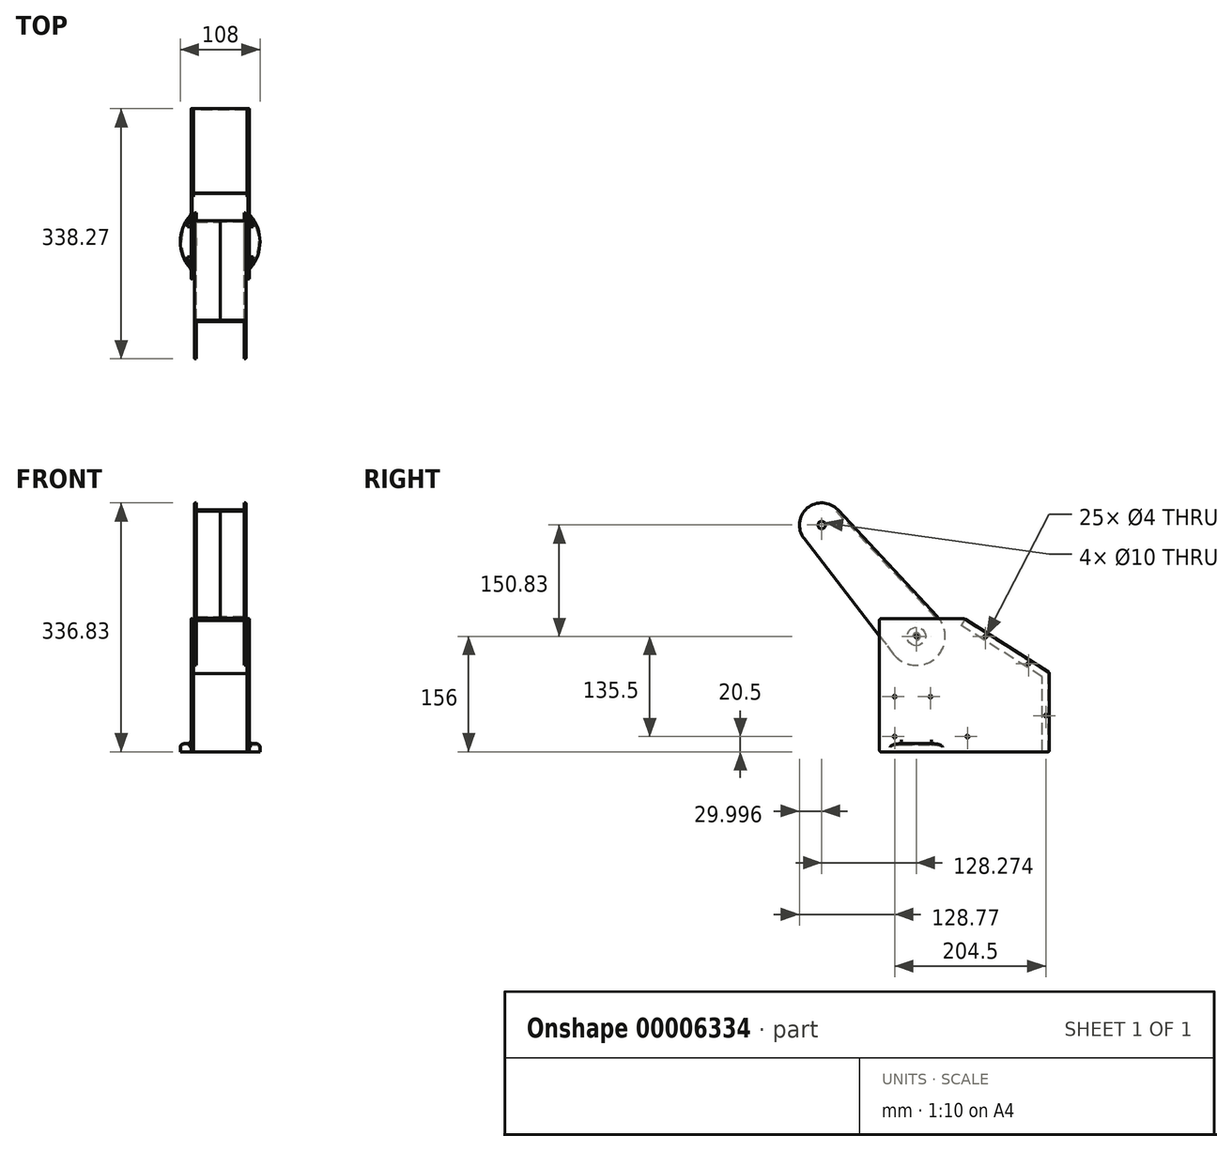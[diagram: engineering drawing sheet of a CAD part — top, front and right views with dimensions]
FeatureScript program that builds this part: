
annotation { "Feature Type Name" : "Feature", "Feature Type Description" : "" }
export const myFeature = defineFeature(function(context is Context, id is Id, definition is map)
    precondition{}
    {
        {
            var Q0;
            Q0=qCreatedBy(makeId("Right.planeOp"),FACE);
            var sketch = newSketch(context, id + "F0", { "sketchPlane" : qUnion([Q0])});
            skLineSegment(sketch, "E0", {"start": v(0, 2) * mm, "end": v(0, 178) * mm});
            skLineSegment(sketch, "E1", {"start": v(2, 180) * mm, "end": v(113.55, 180) * mm});
            skLineSegment(sketch, "E2", {"start": v(116.23, 179.22) * mm, "end": v(229.07, 107.59) * mm});
            skLineSegment(sketch, "E3", {"start": v(230, 105.9) * mm, "end": v(230, 2) * mm});
            skLineSegment(sketch, "E4", {"start": v(228, 0) * mm, "end": v(2, 0) * mm});
            skCircle(sketch, "E5", {"center": v(143.48, 156) * mm, "radius": 2 * mm});
            skCircle(sketch, "E6", {"center": v(201.5, 119.17) * mm, "radius": 2 * mm});
            skCircle(sketch, "E7", {"center": v(225, 49) * mm, "radius": 2 * mm});
            skLineSegment(sketch, "E8", {"start": v(230, 101.08) * mm, "end": v(105.67, 180) * mm, "construction": true});
            skLineSegment(sketch, "E9", {"start": v(225, 110.17) * mm, "end": v(225, 0) * mm, "construction": true});
            skCircle(sketch, "E10", {"center": v(50, 156) * mm, "radius": 2 * mm});
            skCircle(sketch, "E11", {"center": v(20.5, 74.5) * mm, "radius": 2 * mm});
            skCircle(sketch, "E12", {"center": v(69, 74.5) * mm, "radius": 2 * mm});
            skCircle(sketch, "E13", {"center": v(119, 20.5) * mm, "radius": 2 * mm});
            skLineSegment(sketch, "E14", {"start": v(20.5, 180) * mm, "end": v(20.5, 0) * mm, "construction": true});
            skLineSegment(sketch, "E15", {"start": v(0, 20.5) * mm, "end": v(230, 20.5) * mm, "construction": true});
            skCircle(sketch, "E16", {"center": v(20.5, 20.5) * mm, "radius": 2 * mm});
            skLineSegment(sketch, "E17", {"start": v(0, 74.5) * mm, "end": v(69, 74.5) * mm, "construction": true});
            skPoint(sketch, "E18.visualSharp", {"position": v(115, 180) * mm});
            skArc(sketch, "E18.filletArc", {"start": v(116.23, 179.22) * mm, "mid": v(114.94, 179.8) * mm, "end": v(113.55, 180) * mm});
            skPoint(sketch, "E19.visualSharp", {"position": v(0, 180) * mm});
            skArc(sketch, "E19.filletArc", {"start": v(2, 180) * mm, "mid": v(0.59, 179.41) * mm, "end": v(0, 178) * mm});
            skPoint(sketch, "E20.visualSharp", {"position": v(0, 0) * mm});
            skArc(sketch, "E20.filletArc", {"start": v(0, 2) * mm, "mid": v(0.59, 0.59) * mm, "end": v(2, 0) * mm});
            skPoint(sketch, "E21.visualSharp", {"position": v(230, 0) * mm});
            skArc(sketch, "E21.filletArc", {"start": v(228, 0) * mm, "mid": v(229.41, 0.59) * mm, "end": v(230, 2) * mm});
            skPoint(sketch, "E22.visualSharp", {"position": v(230, 107) * mm});
            skArc(sketch, "E22.filletArc", {"start": v(230, 105.9) * mm, "mid": v(229.75, 106.86) * mm, "end": v(229.07, 107.59) * mm});
            skLineSegment(sketch, "E23", {"start": v(0, 156) * mm, "end": v(152.8, 156) * mm, "construction": true});
            skSolve(sketch);
        }
        {
            var Q0;
            Q0=makeQuery(id+"F0.imprint","IMPRINT",FACE,{"disambiguationData":[TD([[makeQuery(id+"F0.imprint","IMPRINT",EDGE,{"derivedFrom":sQuery(id+"F0.wireOp",EDGE,"E0")}),-1.0]])]});
            extrude(context, id + "F1", {"entities" : qUnion([Q0]), "depth" : 1.7 * mm});
        }
        {
            var Q0;
            Q0=makeQuery(id+"F1.opExtrude","CAP_FACE",FACE,{"disambiguationData":[OSD([sQuery(id+"F0.wireOp",EDGE,"E0"),sQuery(id+"F0.wireOp",EDGE,"E1"),sQuery(id+"F0.wireOp",EDGE,"E2"),sQuery(id+"F0.wireOp",EDGE,"E3"),sQuery(id+"F0.wireOp",EDGE,"E4"),sQuery(id+"F0.wireOp",EDGE,"E5"),sQuery(id+"F0.wireOp",EDGE,"E6"),sQuery(id+"F0.wireOp",EDGE,"E7"),sQuery(id+"F0.wireOp",EDGE,"E10"),sQuery(id+"F0.wireOp",EDGE,"E11"),sQuery(id+"F0.wireOp",EDGE,"E12"),sQuery(id+"F0.wireOp",EDGE,"E13"),sQuery(id+"F0.wireOp",EDGE,"E16"),sQuery(id+"F0.wireOp",EDGE,"E18.filletArc"),sQuery(id+"F0.wireOp",EDGE,"E19.filletArc"),sQuery(id+"F0.wireOp",EDGE,"E20.filletArc"),sQuery(id+"F0.wireOp",EDGE,"E21.filletArc"),sQuery(id+"F0.wireOp",EDGE,"E22.filletArc")])],"isStart":true});
            cPlane(context, id + "F2", {"entities" : qUnion([Q0]), "cplaneType" : CPlaneType.OFFSET, "offset" : (79 / 2) * mm, "oppositeDirection" : true, "width" : 150 * mm, "height" : 150 * mm});
        }
        {
            var Q0;
            Q0=qCreatedBy(makeId("Top.planeOp"),FACE);
            var sketch = newSketch(context, id + "F3", { "sketchPlane" : qUnion([Q0])});
            skCircle(sketch, "E24", {"center": v(39.5, 50) * mm, "radius": 54 * mm});
            skSolve(sketch);
        }
        {
            var Q0;
            Q0=makeQuery(id+"F3.imprint","IMPRINT",FACE,{"disambiguationData":[TD([[makeQuery(id+"F3.imprint","IMPRINT",EDGE,{"derivedFrom":sQuery(id+"F3.wireOp",EDGE,"E24")}),1.0]])]});
            extrude(context, id + "F4", {"entities" : qUnion([Q0]), "operationType" : NewBodyOperationType.ADD, "depth" : 11 * mm});
        }
        {
            var Q0;
            {var subQ0=sQuery(id+"F3.wireOp",EDGE,"E24");Q0=makeQuery(id+"F4.boolean.opBoolean","SPLIT",FACE,{"disambiguationData":[TD([makeQuery(id+"F1.opExtrude","CAP_FACE",FACE,{"disambiguationData":[OSD([sQuery(id+"F0.wireOp",EDGE,"E0"),sQuery(id+"F0.wireOp",EDGE,"E1"),sQuery(id+"F0.wireOp",EDGE,"E2"),sQuery(id+"F0.wireOp",EDGE,"E3"),sQuery(id+"F0.wireOp",EDGE,"E4"),sQuery(id+"F0.wireOp",EDGE,"E5"),sQuery(id+"F0.wireOp",EDGE,"E6"),sQuery(id+"F0.wireOp",EDGE,"E7"),sQuery(id+"F0.wireOp",EDGE,"E10"),sQuery(id+"F0.wireOp",EDGE,"E11"),sQuery(id+"F0.wireOp",EDGE,"E12"),sQuery(id+"F0.wireOp",EDGE,"E13"),sQuery(id+"F0.wireOp",EDGE,"E16"),sQuery(id+"F0.wireOp",EDGE,"E18.filletArc"),sQuery(id+"F0.wireOp",EDGE,"E19.filletArc"),sQuery(id+"F0.wireOp",EDGE,"E20.filletArc"),sQuery(id+"F0.wireOp",EDGE,"E21.filletArc"),sQuery(id+"F0.wireOp",EDGE,"E22.filletArc")])],"isStart":false})])],"derivedFrom":makeQuery(id+"F4.opExtrude","CAP_FACE",FACE,{"disambiguationData":[OSD([subQ0])],"isStart":false})});}
            extrude(context, id + "F5", {"entities" : qUnion([Q0]), "operationType" : NewBodyOperationType.REMOVE, "endBound" : BoundingType.UP_TO_NEXT, "oppositeDirection" : true, "depth" : 25 * mm});
        }
        {
            var Q0;
            Q0=makeQuery(id+"F4.boolean.opBoolean","INTERSECT",EDGE,{"disambiguationData":[OD(1.0)],"derivedFrom":[makeQuery(id+"F1.opExtrude","CAP_FACE",FACE,{"disambiguationData":[OSD([sQuery(id+"F0.wireOp",EDGE,"E0"),sQuery(id+"F0.wireOp",EDGE,"E1"),sQuery(id+"F0.wireOp",EDGE,"E2"),sQuery(id+"F0.wireOp",EDGE,"E3"),sQuery(id+"F0.wireOp",EDGE,"E4"),sQuery(id+"F0.wireOp",EDGE,"E5"),sQuery(id+"F0.wireOp",EDGE,"E6"),sQuery(id+"F0.wireOp",EDGE,"E7"),sQuery(id+"F0.wireOp",EDGE,"E10"),sQuery(id+"F0.wireOp",EDGE,"E11"),sQuery(id+"F0.wireOp",EDGE,"E12"),sQuery(id+"F0.wireOp",EDGE,"E13"),sQuery(id+"F0.wireOp",EDGE,"E16"),sQuery(id+"F0.wireOp",EDGE,"E18.filletArc"),sQuery(id+"F0.wireOp",EDGE,"E19.filletArc"),sQuery(id+"F0.wireOp",EDGE,"E20.filletArc"),sQuery(id+"F0.wireOp",EDGE,"E21.filletArc"),sQuery(id+"F0.wireOp",EDGE,"E22.filletArc")])],"isStart":true}),makeQuery(id+"F4.opExtrude","SWEPT_FACE",FACE,{"disambiguationData":[OSD([sQuery(id+"F3.wireOp",EDGE,"E24")])]})]});
            var Q1;
            Q1=makeQuery(id+"F4.boolean.opBoolean","INTERSECT",EDGE,{"derivedFrom":[makeQuery(id+"F1.opExtrude","CAP_FACE",FACE,{"disambiguationData":[OSD([sQuery(id+"F0.wireOp",EDGE,"E0"),sQuery(id+"F0.wireOp",EDGE,"E1"),sQuery(id+"F0.wireOp",EDGE,"E2"),sQuery(id+"F0.wireOp",EDGE,"E3"),sQuery(id+"F0.wireOp",EDGE,"E4"),sQuery(id+"F0.wireOp",EDGE,"E5"),sQuery(id+"F0.wireOp",EDGE,"E6"),sQuery(id+"F0.wireOp",EDGE,"E7"),sQuery(id+"F0.wireOp",EDGE,"E10"),sQuery(id+"F0.wireOp",EDGE,"E11"),sQuery(id+"F0.wireOp",EDGE,"E12"),sQuery(id+"F0.wireOp",EDGE,"E13"),sQuery(id+"F0.wireOp",EDGE,"E16"),sQuery(id+"F0.wireOp",EDGE,"E18.filletArc"),sQuery(id+"F0.wireOp",EDGE,"E19.filletArc"),sQuery(id+"F0.wireOp",EDGE,"E20.filletArc"),sQuery(id+"F0.wireOp",EDGE,"E21.filletArc"),sQuery(id+"F0.wireOp",EDGE,"E22.filletArc")])],"isStart":true}),makeQuery(id+"F4.opExtrude","CAP_FACE",FACE,{"disambiguationData":[OSD([sQuery(id+"F3.wireOp",EDGE,"E24")])],"isStart":false})]});
            var Q2;
            Q2=makeQuery(id+"F4.boolean.opBoolean","INTERSECT",EDGE,{"disambiguationData":[OD(0.0)],"derivedFrom":[makeQuery(id+"F1.opExtrude","CAP_FACE",FACE,{"disambiguationData":[OSD([sQuery(id+"F0.wireOp",EDGE,"E0"),sQuery(id+"F0.wireOp",EDGE,"E1"),sQuery(id+"F0.wireOp",EDGE,"E2"),sQuery(id+"F0.wireOp",EDGE,"E3"),sQuery(id+"F0.wireOp",EDGE,"E4"),sQuery(id+"F0.wireOp",EDGE,"E5"),sQuery(id+"F0.wireOp",EDGE,"E6"),sQuery(id+"F0.wireOp",EDGE,"E7"),sQuery(id+"F0.wireOp",EDGE,"E10"),sQuery(id+"F0.wireOp",EDGE,"E11"),sQuery(id+"F0.wireOp",EDGE,"E12"),sQuery(id+"F0.wireOp",EDGE,"E13"),sQuery(id+"F0.wireOp",EDGE,"E16"),sQuery(id+"F0.wireOp",EDGE,"E18.filletArc"),sQuery(id+"F0.wireOp",EDGE,"E19.filletArc"),sQuery(id+"F0.wireOp",EDGE,"E20.filletArc"),sQuery(id+"F0.wireOp",EDGE,"E21.filletArc"),sQuery(id+"F0.wireOp",EDGE,"E22.filletArc")])],"isStart":true}),makeQuery(id+"F4.opExtrude","SWEPT_FACE",FACE,{"disambiguationData":[OSD([sQuery(id+"F3.wireOp",EDGE,"E24")])]})]});
            var Q3;
            {var subQ0=sQuery(id+"F3.wireOp",EDGE,"E24");Q3=makeQuery(id+"F4.boolean.opBoolean","SPLIT",EDGE,{"disambiguationData":[TD([makeQuery(id+"F1.opExtrude","CAP_FACE",FACE,{"disambiguationData":[OSD([sQuery(id+"F0.wireOp",EDGE,"E0"),sQuery(id+"F0.wireOp",EDGE,"E1"),sQuery(id+"F0.wireOp",EDGE,"E2"),sQuery(id+"F0.wireOp",EDGE,"E3"),sQuery(id+"F0.wireOp",EDGE,"E4"),sQuery(id+"F0.wireOp",EDGE,"E5"),sQuery(id+"F0.wireOp",EDGE,"E6"),sQuery(id+"F0.wireOp",EDGE,"E7"),sQuery(id+"F0.wireOp",EDGE,"E10"),sQuery(id+"F0.wireOp",EDGE,"E11"),sQuery(id+"F0.wireOp",EDGE,"E12"),sQuery(id+"F0.wireOp",EDGE,"E13"),sQuery(id+"F0.wireOp",EDGE,"E16"),sQuery(id+"F0.wireOp",EDGE,"E18.filletArc"),sQuery(id+"F0.wireOp",EDGE,"E19.filletArc"),sQuery(id+"F0.wireOp",EDGE,"E20.filletArc"),sQuery(id+"F0.wireOp",EDGE,"E21.filletArc"),sQuery(id+"F0.wireOp",EDGE,"E22.filletArc")])],"isStart":true})])],"derivedFrom":makeQuery(id+"F4.opExtrude","CAP_EDGE",EDGE,{"disambiguationData":[OSD([subQ0])],"isStart":false})});}
            fillet(context, id + "F6", {"entities" : qUnion([Q0, Q1, Q2, Q3]), "radius" : 5 * mm, "tangentPropagation" : true, "allowEdgeOverflow" : false});
        }
        {
            var Q0;
            {var subQ0=sQuery(id+"F0.wireOp",EDGE,"E22.filletArc");var subQ1=sQuery(id+"F0.wireOp",EDGE,"E21.filletArc");var subQ2=sQuery(id+"F0.wireOp",EDGE,"E20.filletArc");var subQ3=sQuery(id+"F0.wireOp",EDGE,"E19.filletArc");var subQ4=sQuery(id+"F0.wireOp",EDGE,"E18.filletArc");var subQ5=sQuery(id+"F0.wireOp",EDGE,"E16");var subQ6=sQuery(id+"F0.wireOp",EDGE,"E13");var subQ7=sQuery(id+"F0.wireOp",EDGE,"E12");var subQ8=sQuery(id+"F0.wireOp",EDGE,"E11");var subQ9=sQuery(id+"F0.wireOp",EDGE,"E10");var subQ10=sQuery(id+"F0.wireOp",EDGE,"E7");var subQ11=sQuery(id+"F0.wireOp",EDGE,"E6");var subQ12=sQuery(id+"F0.wireOp",EDGE,"E5");var subQ13=sQuery(id+"F0.wireOp",EDGE,"E4");var subQ14=sQuery(id+"F0.wireOp",EDGE,"E3");var subQ15=sQuery(id+"F0.wireOp",EDGE,"E2");var subQ16=sQuery(id+"F0.wireOp",EDGE,"E1");var subQ17=sQuery(id+"F0.wireOp",EDGE,"E0");Q0=makeQuery(id+"F5.boolean.opBoolean","MERGE",FACE,{"derivedFrom":[makeQuery(id+"F1.opExtrude","CAP_FACE",FACE,{"disambiguationData":[OSD([subQ17,subQ16,subQ15,subQ14,subQ13,subQ12,subQ11,subQ10,subQ9,subQ8,subQ7,subQ6,subQ5,subQ4,subQ3,subQ2,subQ1,subQ0])],"isStart":false})],"fromTools":[makeQuery(id+"F5.opExtrude","SWEPT_FACE",FACE,{"disambiguationData":[OSD([subQ17,subQ16,subQ15,subQ14,subQ13,subQ12,subQ11,subQ10,subQ9,subQ8,subQ7,subQ6,subQ5,subQ4,subQ3,subQ2,subQ1,subQ0,sQuery(id+"F3.wireOp",EDGE,"E24")])]})]});}
            var Q1;
            Q1=makeQuery(id+"F4.boolean.opBoolean","MERGE",FACE,{"derivedFrom":[makeQuery(id+"F1.opExtrude","SWEPT_FACE",FACE,{"disambiguationData":[OSD([sQuery(id+"F0.wireOp",EDGE,"E4")])]}),makeQuery(id+"F4.opExtrude","CAP_FACE",FACE,{"disambiguationData":[OSD([sQuery(id+"F3.wireOp",EDGE,"E24")])],"isStart":true})]});
            shell(context, id + "F7", {"entities" : qUnion([Q0, Q1]), "thickness" : 1.7 * mm});
        }
        {
            var Q0;
            {var subQ0=sQuery(id+"F0.wireOp",EDGE,"E22.filletArc");var subQ1=sQuery(id+"F0.wireOp",EDGE,"E21.filletArc");var subQ2=sQuery(id+"F0.wireOp",EDGE,"E20.filletArc");var subQ3=sQuery(id+"F0.wireOp",EDGE,"E19.filletArc");var subQ4=sQuery(id+"F0.wireOp",EDGE,"E18.filletArc");var subQ5=sQuery(id+"F0.wireOp",EDGE,"E16");var subQ6=sQuery(id+"F0.wireOp",EDGE,"E13");var subQ7=sQuery(id+"F0.wireOp",EDGE,"E12");var subQ8=sQuery(id+"F0.wireOp",EDGE,"E11");var subQ9=sQuery(id+"F0.wireOp",EDGE,"E10");var subQ10=sQuery(id+"F0.wireOp",EDGE,"E7");var subQ11=sQuery(id+"F0.wireOp",EDGE,"E6");var subQ12=sQuery(id+"F0.wireOp",EDGE,"E5");var subQ13=sQuery(id+"F0.wireOp",EDGE,"E4");var subQ14=sQuery(id+"F0.wireOp",EDGE,"E3");var subQ15=sQuery(id+"F0.wireOp",EDGE,"E2");var subQ16=sQuery(id+"F0.wireOp",EDGE,"E1");var subQ17=sQuery(id+"F0.wireOp",EDGE,"E0");Q0=makeQuery(id+"F5.boolean.opBoolean","MERGE",FACE,{"derivedFrom":[makeQuery(id+"F1.opExtrude","CAP_FACE",FACE,{"disambiguationData":[OSD([subQ17,subQ16,subQ15,subQ14,subQ13,subQ12,subQ11,subQ10,subQ9,subQ8,subQ7,subQ6,subQ5,subQ4,subQ3,subQ2,subQ1,subQ0])],"isStart":false})],"fromTools":[makeQuery(id+"F5.opExtrude","SWEPT_FACE",FACE,{"disambiguationData":[OSD([subQ17,subQ16,subQ15,subQ14,subQ13,subQ12,subQ11,subQ10,subQ9,subQ8,subQ7,subQ6,subQ5,subQ4,subQ3,subQ2,subQ1,subQ0,sQuery(id+"F3.wireOp",EDGE,"E24")])]})]});}
            var sketch = newSketch(context, id + "F8", { "sketchPlane" : qUnion([Q0])});
            skLineSegment(sketch, "E25", {"start": v(116.23, 179.22) * mm, "end": v(230, 107) * mm});
            skLineSegment(sketch, "E26", {"start": v(230, 107) * mm, "end": v(230, 0) * mm});
            skLineSegment(sketch, "E27", {"start": v(230, 0) * mm, "end": v(220, 0) * mm});
            skLineSegment(sketch, "E28", {"start": v(220, 0) * mm, "end": v(220, 101.5) * mm});
            skLineSegment(sketch, "E29", {"start": v(220, 101.5) * mm, "end": v(110.87, 170.78) * mm});
            skLineSegment(sketch, "E30", {"start": v(110.87, 170.78) * mm, "end": v(116.23, 179.22) * mm});
            skCircle(sketch, "E31", {"center": v(143.48, 156) * mm, "radius": 2 * mm});
            skCircle(sketch, "E32", {"center": v(201.5, 119.17) * mm, "radius": 2 * mm});
            skCircle(sketch, "E33", {"center": v(225, 49) * mm, "radius": 2 * mm});
            skSolve(sketch);
        }
        {
            var Q0;
            {var subQ5=sQuery(id+"F8.wireOp",EDGE,"E28");Q0=makeQuery(id+"F8.imprint","IMPRINT",FACE,{"disambiguationData":[TD([[makeQuery(id+"F8.imprint","IMPRINT",EDGE,{"derivedFrom":subQ5}),-1.0]])]});}
            extrude(context, id + "F9", {"entities" : qUnion([Q0]), "depth" : 1.7 * mm});
        }
        {
            var Q0;
            {var subQ0=sQuery(id+"F0.wireOp",EDGE,"E22.filletArc");var subQ1=sQuery(id+"F0.wireOp",EDGE,"E21.filletArc");var subQ2=sQuery(id+"F0.wireOp",EDGE,"E20.filletArc");var subQ3=sQuery(id+"F0.wireOp",EDGE,"E19.filletArc");var subQ4=sQuery(id+"F0.wireOp",EDGE,"E18.filletArc");var subQ5=sQuery(id+"F0.wireOp",EDGE,"E16");var subQ6=sQuery(id+"F0.wireOp",EDGE,"E13");var subQ7=sQuery(id+"F0.wireOp",EDGE,"E12");var subQ8=sQuery(id+"F0.wireOp",EDGE,"E11");var subQ9=sQuery(id+"F0.wireOp",EDGE,"E10");var subQ10=sQuery(id+"F0.wireOp",EDGE,"E7");var subQ11=sQuery(id+"F0.wireOp",EDGE,"E6");var subQ12=sQuery(id+"F0.wireOp",EDGE,"E5");var subQ13=sQuery(id+"F0.wireOp",EDGE,"E4");var subQ14=sQuery(id+"F0.wireOp",EDGE,"E3");var subQ15=sQuery(id+"F0.wireOp",EDGE,"E2");var subQ16=sQuery(id+"F0.wireOp",EDGE,"E1");var subQ17=sQuery(id+"F0.wireOp",EDGE,"E0");Q0=makeQuery(id+"F5.boolean.opBoolean","MERGE",FACE,{"derivedFrom":[makeQuery(id+"F1.opExtrude","CAP_FACE",FACE,{"disambiguationData":[OSD([subQ17,subQ16,subQ15,subQ14,subQ13,subQ12,subQ11,subQ10,subQ9,subQ8,subQ7,subQ6,subQ5,subQ4,subQ3,subQ2,subQ1,subQ0])],"isStart":false})],"fromTools":[makeQuery(id+"F5.opExtrude","SWEPT_FACE",FACE,{"disambiguationData":[OSD([subQ17,subQ16,subQ15,subQ14,subQ13,subQ12,subQ11,subQ10,subQ9,subQ8,subQ7,subQ6,subQ5,subQ4,subQ3,subQ2,subQ1,subQ0,sQuery(id+"F3.wireOp",EDGE,"E24")])]})]});}
            var sketch = newSketch(context, id + "F10", { "sketchPlane" : qUnion([Q0])});
            skCircle(sketch, "E34", {"center": v(50, 156) * mm, "radius": 2 * mm});
            skCircle(sketch, "E35", {"center": v(50, 156) * mm, "radius": 12.5 * mm});
            skSolve(sketch);
        }
        {
            var Q0;
            Q0=makeQuery(id+"F10.imprint","IMPRINT",FACE,{"disambiguationData":[TD([[makeQuery(id+"F10.imprint","IMPRINT",EDGE,{"derivedFrom":sQuery(id+"F10.wireOp",EDGE,"E34")}),-1.0]])]});
            extrude(context, id + "F11", {"entities" : qUnion([Q0]), "depth" : 3 * mm});
        }
        {
            var Q0;
            Q0=makeQuery(id+"F11.opExtrude","CAP_EDGE",EDGE,{"disambiguationData":[OSD([sQuery(id+"F10.wireOp",EDGE,"E35")])],"isStart":true});
            var Q1;
            Q1=makeQuery(id+"F11.opExtrude","CAP_EDGE",EDGE,{"disambiguationData":[OSD([sQuery(id+"F10.wireOp",EDGE,"E35")])],"isStart":false});
            fillet(context, id + "F12", {"entities" : qUnion([Q0, Q1]), "radius" : 1.5 * mm, "tangentPropagation" : true, "allowEdgeOverflow" : false});
        }
        {
            var Q0;
            Q0=makeQuery(id+"F1.opExtrude","SWEPT_BODY",BODY,{"disambiguationData":[OSD([sQuery(id+"F0.wireOp",EDGE,"E0"),sQuery(id+"F0.wireOp",EDGE,"E1"),sQuery(id+"F0.wireOp",EDGE,"E2"),sQuery(id+"F0.wireOp",EDGE,"E3"),sQuery(id+"F0.wireOp",EDGE,"E4"),sQuery(id+"F0.wireOp",EDGE,"E5"),sQuery(id+"F0.wireOp",EDGE,"E6"),sQuery(id+"F0.wireOp",EDGE,"E7"),sQuery(id+"F0.wireOp",EDGE,"E10"),sQuery(id+"F0.wireOp",EDGE,"E11"),sQuery(id+"F0.wireOp",EDGE,"E12"),sQuery(id+"F0.wireOp",EDGE,"E13"),sQuery(id+"F0.wireOp",EDGE,"E16"),sQuery(id+"F0.wireOp",EDGE,"E18.filletArc"),sQuery(id+"F0.wireOp",EDGE,"E19.filletArc"),sQuery(id+"F0.wireOp",EDGE,"E20.filletArc"),sQuery(id+"F0.wireOp",EDGE,"E21.filletArc"),sQuery(id+"F0.wireOp",EDGE,"E22.filletArc")])]});
            var Q1;
            Q1=makeQuery(id+"F9.opExtrude","SWEPT_BODY",BODY,{"disambiguationData":[OSD([sQuery(id+"F0.wireOp",EDGE,"E21.filletArc"),sQuery(id+"F0.wireOp",EDGE,"E22.filletArc"),sQuery(id+"F8.wireOp",EDGE,"E25"),sQuery(id+"F8.wireOp",EDGE,"E26"),sQuery(id+"F8.wireOp",EDGE,"E27"),sQuery(id+"F8.wireOp",EDGE,"E28"),sQuery(id+"F8.wireOp",EDGE,"E29"),sQuery(id+"F8.wireOp",EDGE,"E30"),sQuery(id+"F8.wireOp",EDGE,"E31"),sQuery(id+"F8.wireOp",EDGE,"E32"),sQuery(id+"F8.wireOp",EDGE,"E33")])]});
            var Q2;
            Q2=makeQuery(id+"F11.opExtrude","SWEPT_BODY",BODY,{"disambiguationData":[OSD([sQuery(id+"F10.wireOp",EDGE,"E34"),sQuery(id+"F10.wireOp",EDGE,"E35")])]});
            var Q3;
            Q3=qCreatedBy(id+"F2.planeOp",FACE);
            mirror(context, id + "F13", {"entities" : qUnion([Q0, Q1, Q2]), "mirrorPlane" : qUnion([Q3])});
        }
        {
            var Q0;
            Q0=makeQuery(id+"F9.opExtrude","CAP_FACE",FACE,{"disambiguationData":[OSD([sQuery(id+"F0.wireOp",EDGE,"E21.filletArc"),sQuery(id+"F0.wireOp",EDGE,"E22.filletArc"),sQuery(id+"F8.wireOp",EDGE,"E25"),sQuery(id+"F8.wireOp",EDGE,"E26"),sQuery(id+"F8.wireOp",EDGE,"E27"),sQuery(id+"F8.wireOp",EDGE,"E28"),sQuery(id+"F8.wireOp",EDGE,"E29"),sQuery(id+"F8.wireOp",EDGE,"E30"),sQuery(id+"F8.wireOp",EDGE,"E31"),sQuery(id+"F8.wireOp",EDGE,"E32"),sQuery(id+"F8.wireOp",EDGE,"E33")])],"isStart":false});
            var sketch = newSketch(context, id + "F14", { "sketchPlane" : qUnion([Q0])});
            skLineSegment(sketch, "E36", {"start": v(115.32, 177.79) * mm, "end": v(228.3, 106.07) * mm});
            skLineSegment(sketch, "E37", {"start": v(228.3, 106.07) * mm, "end": v(228.3, 0) * mm});
            skSolve(sketch);
        }
        {
            var Q0;
            Q0 = qSketchRegion(id + "F14", true);
            var Q1;
            {var subQ5=sQuery(id+"F14.wireOp",EDGE,"E36");Q1=makeQuery(id+"F14.imprint","IMPRINT",FACE,{"disambiguationData":[TD([[makeQuery(id+"F14.imprint","IMPRINT",EDGE,{"derivedFrom":subQ5}),1.0]])]});}
            var Q2;
            Q2=makeQuery(id+"F13.opPattern","COPY",FACE,{"derivedFrom":makeQuery(id+"F9.opExtrude","CAP_FACE",FACE,{"disambiguationData":[OSD([sQuery(id+"F0.wireOp",EDGE,"E21.filletArc"),sQuery(id+"F0.wireOp",EDGE,"E22.filletArc"),sQuery(id+"F8.wireOp",EDGE,"E25"),sQuery(id+"F8.wireOp",EDGE,"E26"),sQuery(id+"F8.wireOp",EDGE,"E27"),sQuery(id+"F8.wireOp",EDGE,"E28"),sQuery(id+"F8.wireOp",EDGE,"E29"),sQuery(id+"F8.wireOp",EDGE,"E30"),sQuery(id+"F8.wireOp",EDGE,"E31"),sQuery(id+"F8.wireOp",EDGE,"E32"),sQuery(id+"F8.wireOp",EDGE,"E33")])],"isStart":false}),"instanceName":"1"});
            extrude(context, id + "F15", {"entities" : qUnion([Q0, Q1]), "endBound" : BoundingType.UP_TO_SURFACE, "endBoundEntityFace" : qUnion([Q2]), "depth" : 25 * mm});
        }
        {
            var Q0;
            Q0=makeQuery(id+"F15.opExtrude","CAP_EDGE",EDGE,{"disambiguationData":[OSD([sQuery(id+"F14.wireOp",EDGE,"E36")])],"isStart":true});
            var Q1;
            Q1=makeQuery(id+"F9.opExtrude","CAP_EDGE",EDGE,{"disambiguationData":[OSD([sQuery(id+"F8.wireOp",EDGE,"E25")])],"isStart":true});
            var Q2;
            Q2=makeQuery(id+"F15.opExtrude","CAP_EDGE",EDGE,{"disambiguationData":[OSD([sQuery(id+"F14.wireOp",EDGE,"E37")])],"isStart":true});
            var Q3;
            Q3=makeQuery(id+"F9.opExtrude","CAP_EDGE",EDGE,{"disambiguationData":[OSD([sQuery(id+"F8.wireOp",EDGE,"E26")])],"isStart":true});
            var Q4;
            Q4=makeQuery(id+"F15.opExtrude","CAP_EDGE",EDGE,{"disambiguationData":[OSD([sQuery(id+"F14.wireOp",EDGE,"E36")])],"isStart":false});
            var Q5;
            Q5=makeQuery(id+"F15.opExtrude","CAP_EDGE",EDGE,{"disambiguationData":[OSD([sQuery(id+"F14.wireOp",EDGE,"E37")])],"isStart":false});
            var Q6;
            Q6=makeQuery(id+"F13.opPattern","COPY",EDGE,{"derivedFrom":makeQuery(id+"F9.opExtrude","CAP_EDGE",EDGE,{"disambiguationData":[OSD([sQuery(id+"F8.wireOp",EDGE,"E26")])],"isStart":true}),"instanceName":"1"});
            var Q7;
            Q7=makeQuery(id+"F13.opPattern","COPY",EDGE,{"derivedFrom":makeQuery(id+"F9.opExtrude","CAP_EDGE",EDGE,{"disambiguationData":[OSD([sQuery(id+"F8.wireOp",EDGE,"E25")])],"isStart":true}),"instanceName":"1"});
            fillet(context, id + "F16", {"entities" : qUnion([Q0, Q1, Q2, Q3, Q4, Q5, Q6, Q7]), "radius" : 1 * mm, "tangentPropagation" : true, "allowEdgeOverflow" : false});
        }
        {
            var Q0;
            Q0=makeQuery(id+"F11.opExtrude","SWEPT_BODY",BODY,{"disambiguationData":[OSD([sQuery(id+"F10.wireOp",EDGE,"E34"),sQuery(id+"F10.wireOp",EDGE,"E35")])]});
            var Q1;
            Q1=qCreatedBy(id+"F2.planeOp",FACE);
            mirror(context, id + "F17", {"entities" : qUnion([Q0]), "mirrorPlane" : qUnion([Q1])});
        }
        {
            var Q0;
            Q0=qCreatedBy(id+"F2.planeOp",FACE);
            var sketch = newSketch(context, id + "F18", { "sketchPlane" : qUnion([Q0])});
            skCircle(sketch, "E38", {"center": v(-50, 156) * mm, "radius": 5 * mm});
            skCircle(sketch, "E39", {"center": v(-50, 156) * mm, "radius": 2 * mm});
            skCircle(sketch, "E40", {"center": v(-50, 156) * mm, "radius": 39 * mm});
            skCircle(sketch, "E41", {"center": v(78.27, 306.83) * mm, "radius": 30 * mm});
            skCircle(sketch, "E42", {"center": v(78.27, 306.83) * mm, "radius": 5 * mm});
            skCircle(sketch, "E43", {"center": v(78.27, 306.83) * mm, "radius": 2 * mm});
            skLineSegment(sketch, "E44", {"start": v(-19.17, 132.11) * mm, "end": v(101.99, 288.45) * mm});
            skLineSegment(sketch, "E45", {"start": v(-78.53, 182.6) * mm, "end": v(56.33, 327.28) * mm});
            skCircle(sketch, "E46", {"center": v(221.31, 265.1) * mm, "radius": 2 * mm});
            skCircle(sketch, "E47", {"center": v(221.31, 265.1) * mm, "radius": 5 * mm});
            skCircle(sketch, "E48", {"center": v(221.31, 265.1) * mm, "radius": 20.5 * mm});
            skLineSegment(sketch, "E49", {"start": v(71.73, 277.55) * mm, "end": v(216.84, 245.1) * mm});
            skLineSegment(sketch, "E50", {"start": v(88.5, 335.04) * mm, "end": v(228.3, 284.38) * mm});
            skSolve(sketch);
        }
        {
            var Q0;
            Q0=makeQuery(id+"F18.imprint","IMPRINT",FACE,{"disambiguationData":[TD([[makeQuery(id+"F18.imprint","IMPRINT",EDGE,{"derivedFrom":sQuery(id+"F18.wireOp",EDGE,"E38")}),-1.0]])]});
            var Q1;
            {var subQ5=sQuery(id+"F18.wireOp",EDGE,"E45");Q1=makeQuery(id+"F18.imprint","IMPRINT",FACE,{"disambiguationData":[TD([[makeQuery(id+"F18.imprint","IMPRINT",EDGE,{"derivedFrom":subQ5}),-1.0]])]});}
            var Q2;
            Q2=makeQuery(id+"F18.imprint","IMPRINT",FACE,{"disambiguationData":[TD([[makeQuery(id+"F18.imprint","IMPRINT",EDGE,{"derivedFrom":sQuery(id+"F18.wireOp",EDGE,"E42")}),-1.0]])]});
            var Q3;
            {var subQ1=sQuery(id+"F18.wireOp",EDGE,"E44");var subQ3=sQuery(id+"F18.wireOp",EDGE,"E41");var subQ5=makeQuery(id+"F18.imprint","INTERSECT",VERTEX,{"derivedFrom":[subQ3,subQ1]});Q3=makeQuery(id+"F18.imprint","IMPRINT",FACE,{"disambiguationData":[TD([[makeQuery(id+"F18.imprint","IMPRINT",EDGE,{"disambiguationData":[TD([[subQ5,1.0]])],"derivedFrom":subQ3}),-1.0]])]});}
            var Q4;
            Q4=makeQuery(id+"F11.opExtrude","CAP_FACE",FACE,{"disambiguationData":[OSD([sQuery(id+"F10.wireOp",EDGE,"E34"),sQuery(id+"F10.wireOp",EDGE,"E35")])],"isStart":false});
            extrude(context, id + "F19", {"entities" : qUnion([Q0, Q1, Q2, Q3]), "endBound" : BoundingType.UP_TO_SURFACE, "endBoundEntityFace" : qUnion([Q4]), "depth" : 25 * mm});
        }
        {
            var Q0;
            Q0=makeQuery(id+"F19.opExtrude","SWEPT_FACE",FACE,{"disambiguationData":[OSD([sQuery(id+"F18.wireOp",EDGE,"E44")])]});
            var Q1;
            Q1=makeQuery(id+"F19.opExtrude","SWEPT_FACE",FACE,{"disambiguationData":[OSD([sQuery(id+"F18.wireOp",EDGE,"E40")])]});
            var Q2;
            Q2=makeQuery(id+"F19.opExtrude","CAP_FACE",FACE,{"disambiguationData":[OSD([sQuery(id+"F18.wireOp",EDGE,"E38"),sQuery(id+"F18.wireOp",EDGE,"E40"),sQuery(id+"F18.wireOp",EDGE,"E41"),sQuery(id+"F18.wireOp",EDGE,"E42"),sQuery(id+"F18.wireOp",EDGE,"E44"),sQuery(id+"F18.wireOp",EDGE,"E45")])],"isStart":true});
            var Q3;
            Q3=makeQuery(id+"F19.opExtrude","SWEPT_FACE",FACE,{"disambiguationData":[OSD([sQuery(id+"F18.wireOp",EDGE,"E41")])]});
            var Q4;
            Q4=makeQuery(id+"F19.opExtrude","SWEPT_FACE",FACE,{"disambiguationData":[OSD([sQuery(id+"F18.wireOp",EDGE,"E42")])]});
            var Q5;
            Q5=makeQuery(id+"F19.opExtrude","SWEPT_FACE",FACE,{"disambiguationData":[OSD([sQuery(id+"F18.wireOp",EDGE,"E38")])]});
            shell(context, id + "F20", {"entities" : qUnion([Q0, Q1, Q2, Q3, Q4, Q5]), "thickness" : 2.5 * mm});
        }
        {
            var Q0;
            Q0=makeQuery(id+"F19.opExtrude","CAP_EDGE",EDGE,{"disambiguationData":[OSD([sQuery(id+"F18.wireOp",EDGE,"E45")])],"isStart":false});
            fillet(context, id + "F21", {"entities" : qUnion([Q0]), "radius" : 1 * mm, "tangentPropagation" : true, "allowEdgeOverflow" : false});
        }
        {
            var Q0;
            Q0=makeQuery(id+"F19.opExtrude","SWEPT_BODY",BODY,{"disambiguationData":[OSD([sQuery(id+"F18.wireOp",EDGE,"E38"),sQuery(id+"F18.wireOp",EDGE,"E40"),sQuery(id+"F18.wireOp",EDGE,"E41"),sQuery(id+"F18.wireOp",EDGE,"E42"),sQuery(id+"F18.wireOp",EDGE,"E44"),sQuery(id+"F18.wireOp",EDGE,"E45")])]});
            var Q1;
            Q1=qCreatedBy(id+"F2.planeOp",FACE);
            mirror(context, id + "F22", {"entities" : qUnion([Q0]), "mirrorPlane" : qUnion([Q1])});
        }
    });
